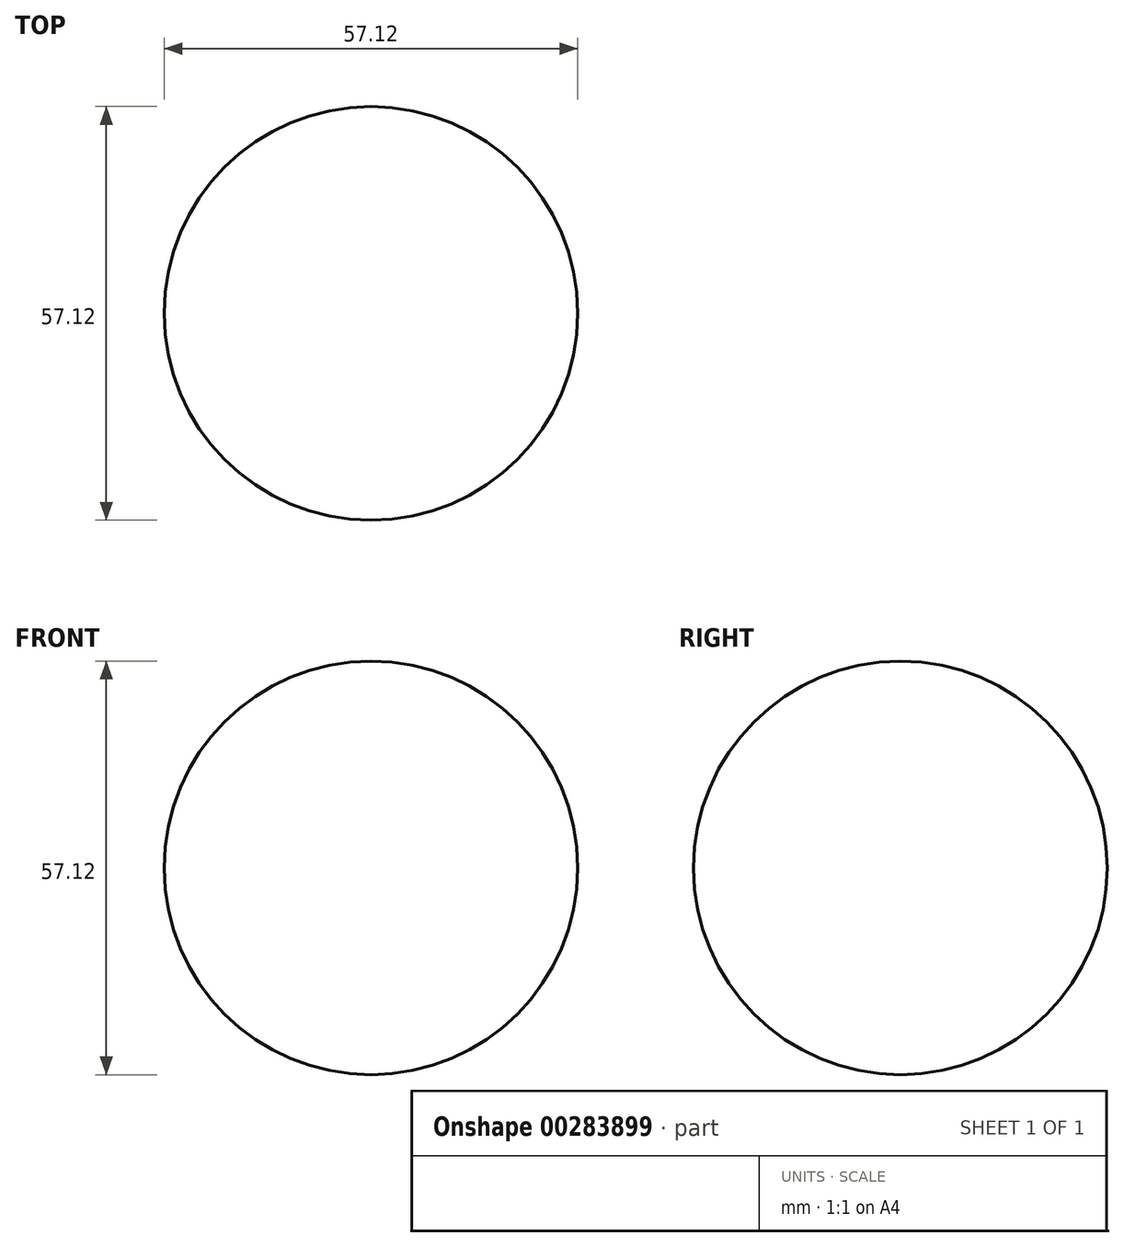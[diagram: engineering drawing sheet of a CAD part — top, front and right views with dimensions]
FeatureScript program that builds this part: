
annotation { "Feature Type Name" : "Feature", "Feature Type Description" : "" }
export const myFeature = defineFeature(function(context is Context, id is Id, definition is map)
    precondition{}
    {
        {
            var Q0;
            Q0=qCreatedBy(makeId("Front.planeOp"),FACE);
            var sketch = newSketch(context, id + "F0", { "sketchPlane" : qUnion([Q0])});
            skArc(sketch, "E0", {"start": v(0, 28.56) * mm, "mid": v(-28.56, 0) * mm, "end": v(0, -28.56) * mm});
            skLineSegment(sketch, "E1", {"start": v(0, 28.56) * mm, "end": v(0, -28.56) * mm});
            skSolve(sketch);
        }
        {
            var Q0;
            Q0=makeQuery(id+"F0.imprint","IMPRINT",FACE,{"disambiguationData":[TD([[makeQuery(id+"F0.imprint","IMPRINT",EDGE,{"derivedFrom":sQuery(id+"F0.wireOp",EDGE,"E0")}),1.0]])]});
            var Q1;
            Q1=sQuery(id+"F0.wireOp",EDGE,"E1");
            revolve(context, id + "F1", {"entities" : qUnion([Q0]), "axis" : qUnion([Q1]), "revolveType" : RevolveType.FULL});
        }
    });
